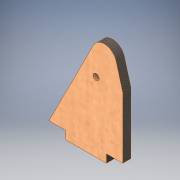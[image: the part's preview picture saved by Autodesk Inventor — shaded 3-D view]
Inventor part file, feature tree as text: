
AUTODESK INVENTOR PART (.ipt)
format: ipt  version: 2019 (Build 230136000, 136)  size: 134,144 bytes
history: native  units: mm
features: extrude x2, sketch x2, other x1
ambient origin geometry x8: Origin, YZ Plane, XZ Plane, XY Plane, X Axis, Y Axis, Z Axis, Center Point
bodies: Body1 (feature_tree)
feature tree (5):
  other  "Твердое тело1"
  extrude  "Выдавливание1"  Depth=6.0mm
  extrude  "Выдавливание2"  Depth=40.0mm
  sketch  "Эскиз1"
  sketch  "Эскиз2"
